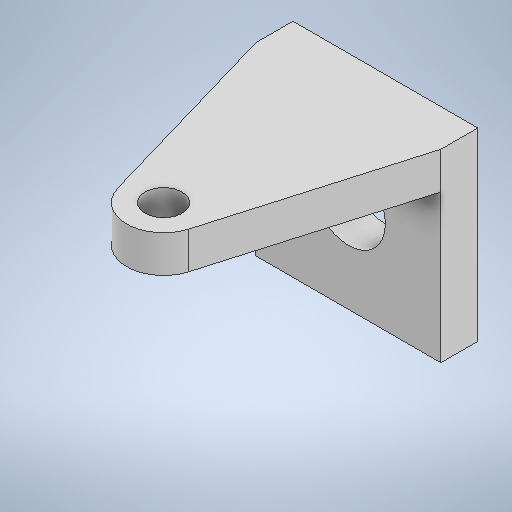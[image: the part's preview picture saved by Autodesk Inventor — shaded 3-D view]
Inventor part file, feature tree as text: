
AUTODESK INVENTOR PART (.ipt)
format: ipt  version: 2025.2 (Build 292293000, 293)  size: 286,208 bytes
history: native  units: in
note: dims shown in document units (in); Inventor stores cm internally (conversion verified against a paired STEP export)
features: extrude x2, sketch x2, plane x1, other x1
ambient origin geometry x8: Origin, YZ Plane, XZ Plane, XY Plane, X Axis, Y Axis, Z Axis, Center Point
bodies: Solid1 (feature_tree)
feature tree (6):
  extrude  "Extrusion1"  Depth=1.9685in
  plane  "Work Plane1"
  extrude  "Extrusion2"  Depth=0.3937in TaperAngle=0.0deg
  sketch  "Sketch1"  dims[d6=1.9685in d7=1.9685in]
  other  "Image1"
  sketch  "Sketch2"  dims[d8=0.7874in d9=0.3937in d10=0.0in d12=0.9843in d13=0.7874in d14=0.3937in d15=1.9685in d17=0.3937in d18=0.0in]
